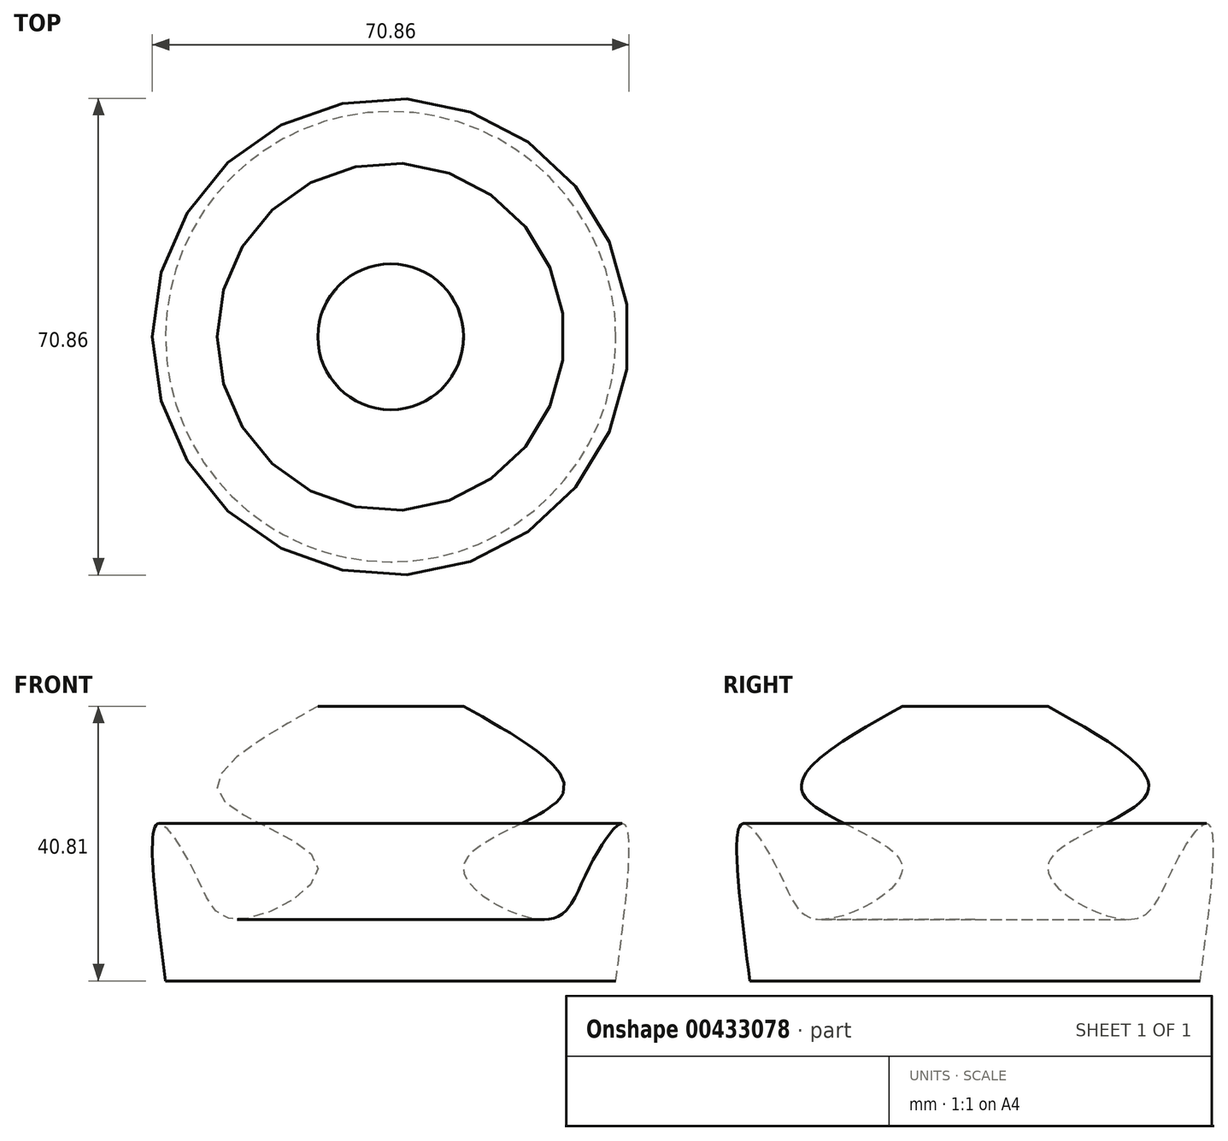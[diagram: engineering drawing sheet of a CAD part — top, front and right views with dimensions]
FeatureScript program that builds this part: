
annotation { "Feature Type Name" : "Feature", "Feature Type Description" : "" }
export const myFeature = defineFeature(function(context is Context, id is Id, definition is map)
    precondition{}
    {
        {
            var Q0;
            Q0=qCreatedBy(makeId("Front.planeOp"),FACE);
            var sketch = newSketch(context, id + "F0", { "sketchPlane" : qUnion([Q0])});
            skLineSegment(sketch, "E0", {"start": v(0, 0) * mm, "end": v(0, 40.81) * mm});
            skLineSegment(sketch, "E1", {"start": v(0, 0) * mm, "end": v(33.47, 0) * mm});
            skLineSegment(sketch, "E2", {"start": v(0, 40.81) * mm, "end": v(10.84, 40.81) * mm});
            skFitSpline(sketch, "E3", {"points": [v(10.84, 40.81) * mm, v(25.46, 27.58) * mm, v(10.84, 17.13) * mm, v(23.02, 9.12) * mm, v(28.94, 15.74) * mm, v(34.52, 23.4) * mm, v(33.47, 0) * mm], "startDerivative": vector(133.18, -74.46) * mm, "endDerivative": vector(-21.57, -166.9) * mm});
            skSolve(sketch);
        }
        {
            var Q0;
            Q0=makeQuery(id+"F0.imprint","IMPRINT",FACE,{"disambiguationData":[TD([[makeQuery(id+"F0.imprint","IMPRINT",EDGE,{"derivedFrom":sQuery(id+"F0.wireOp",EDGE,"E0")}),-1.0]])]});
            var Q1;
            Q1=sQuery(id+"F0.wireOp",EDGE,"E0");
            revolve(context, id + "F1", {"entities" : qUnion([Q0]), "axis" : qUnion([Q1]), "revolveType" : RevolveType.FULL});
        }
    });
